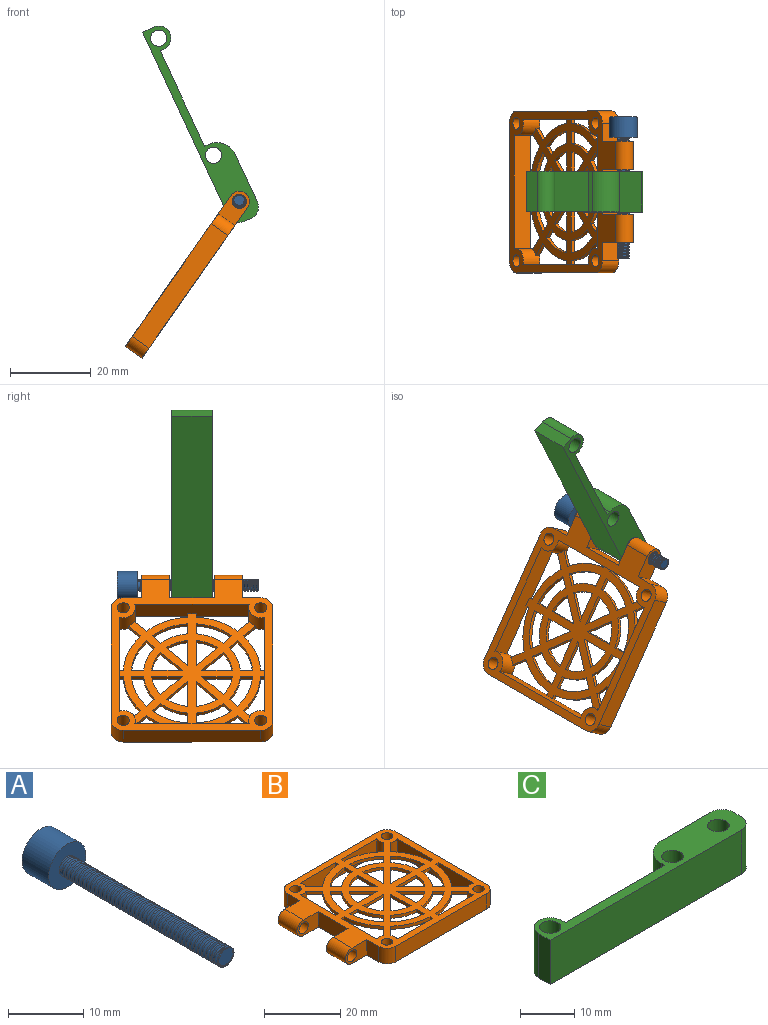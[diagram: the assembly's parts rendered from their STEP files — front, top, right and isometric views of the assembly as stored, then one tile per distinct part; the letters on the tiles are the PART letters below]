
ASSEMBLY  parts=3 mates=2
PART A: 27 faces, bbox 7x35.3x7 mm
  f0: cylinder r=1.5mm len=30mm, axis (0,1,0), area 72mm2, adj f2,f4,f24,f25,f26
  f1: plane 7x7mm, normal (0,1,0), area 16.8mm2, adj f3,f12,f13,f14,f15,f16,f17
  f2: plane 2.88x2.54mm, normal (0,-1,0), area 5.8mm2, adj f0,f24,f25
  f3: cylinder r=3.5mm len=7mm, axis (0,1,0), area 110mm2, adj f1,f4
  f4: plane 7x7mm, normal (0,-1,0), area 31.4mm2, adj f0,f3
  f5: plane 3x1.99mm, normal (-0.5,0,-0.86), area 6.9mm2, adj f6,f10,f13,f19
  f6: plane 3x2.31mm, normal (-1,0,0.01), area 6.9mm2, adj f5,f7,f12,f18
  f7: plane 3x2.01mm, normal (-0.5,0,0.87), area 6.9mm2, adj f6,f8,f14,f20
  f8: plane 3x1.99mm, normal (0.5,0,0.86), area 6.9mm2, adj f7,f9,f16,f22
  f9: plane 3x2.31mm, normal (1,0,-0.01), area 6.9mm2, adj f8,f10,f17,f23
  f10: plane 3x2.01mm, normal (0.5,0,-0.87), area 6.9mm2, adj f5,f9,f15,f21
  f11: plane 3.46x3.01mm, normal (0,1,0), area 7.8mm2, adj f18,f19,f20,f21,f22,f23
  f12: cylinder r=0.5mm len=2.89mm, axis (-0.01,0,-1), area 2mm2, adj f1,f6,f13,f14
  f13: cylinder r=0.5mm len=2.74mm, axis (0.86,0,-0.5), area 2mm2, adj f1,f5,f12,f15
  f14: cylinder r=0.5mm len=2.76mm, axis (-0.87,0,-0.5), area 2mm2, adj f1,f7,f12,f16
  f15: cylinder r=0.5mm len=2.76mm, axis (0.87,0,0.5), area 2mm2, adj f1,f10,f13,f17
  f16: cylinder r=0.5mm len=2.74mm, axis (-0.86,0,0.5), area 2mm2, adj f1,f8,f14,f17
  f17: cylinder r=0.5mm len=2.89mm, axis (0.01,0,1), area 2mm2, adj f1,f9,f15,f16
  f18: cylinder r=0.5mm len=2.31mm, axis (-0.01,0,-1), area 1.6mm2, adj f6,f11,f19,f20
  f19: cylinder r=0.5mm len=2.25mm, axis (0.86,0,-0.5), area 1.6mm2, adj f5,f11,f18,f21
  f20: cylinder r=0.5mm len=2.25mm, axis (-0.87,0,-0.5), area 1.6mm2, adj f7,f11,f18,f22
  f21: cylinder r=0.5mm len=2.25mm, axis (0.87,0,0.5), area 1.6mm2, adj f10,f11,f19,f23
  f22: cylinder r=0.5mm len=2.25mm, axis (-0.86,0,0.5), area 1.6mm2, adj f8,f11,f20,f23
  f23: cylinder r=0.5mm len=2.31mm, axis (0.01,0,1), area 1.6mm2, adj f9,f11,f21,f22
  f24: bspline ~30.18x3.46mm, area 167.6mm2, adj f0,f2,f25,f26
  f25: bspline ~30.14x3.46mm, area 176.2mm2, adj f0,f2,f24,f26
  f26: plane 0.5x0.45mm, normal (0,0,1), area 0.1mm2, adj f0,f24,f25
PART B: 113 faces, bbox 48x40x5 mm
  f0: cylinder r=3mm len=5mm, axis (0,0,-1), area 31.7mm2, adj f13,f14,f22,f23,f83,f84,f112
  f1: plane 28.34x5mm, normal (0,-1,0), area 139.7mm2, adj f2,f15,f22,f23,f74,f75,f112
  f2: cylinder r=3mm len=5mm, axis (0,0,-1), area 31.7mm2, adj f1,f3,f22,f23,f71,f72,f112
  f3: plane 28.34x5mm, normal (-1,0,0), area 139.7mm2, adj f2,f20,f22,f23,f68,f69,f112
  f4: plane 11x5mm, normal (-1,0,0), area 55mm2, adj f22,f23,f24,f26
  f5: plane 5x4.5mm, normal (-1,0,0), area 22.5mm2, adj f12,f22,f23,f25
  f6: cylinder r=3mm len=5mm, axis (0,0,-1), area 23.6mm2, adj f7,f21,f22,f23
  f7: plane 34x5mm, normal (0,-1,0), area 170mm2, adj f6,f8,f22,f23
  f8: cylinder r=3mm len=5mm, axis (0,0,-1), area 23.6mm2, adj f7,f9,f22,f23
  f9: plane 34x5mm, normal (1,0,0), area 170mm2, adj f8,f10,f22,f23
  f10: cylinder r=3mm len=5mm, axis (0,0,-1), area 23.6mm2, adj f9,f11,f22,f23
  f11: plane 34x5mm, normal (0,1,0), area 170mm2, adj f10,f12,f22,f23
  f12: cylinder r=3mm len=5mm, axis (0,0,-1), area 23.6mm2, adj f5,f11,f22,f23
  f13: plane 28.34x5mm, normal (0,1,0), area 139.7mm2, adj f0,f20,f22,f23,f86,f87,f112
  f14: plane 28.34x5mm, normal (1,0,0), area 139.7mm2, adj f0,f15,f22,f23,f80,f81,f112
  f15: cylinder r=3mm len=5mm, axis (0,0,-1), area 31.7mm2, adj f1,f14,f22,f23,f77,f78,f112
  f16: cylinder r=1.5mm len=5mm, axis (0,0,-1), area 47.1mm2, adj f22,f23
  f17: cylinder r=1.5mm len=5mm, axis (0,0,-1), area 47.1mm2, adj f22,f23
  f18: cylinder r=1.5mm len=5mm, axis (0,0,-1), area 47.1mm2, adj f22,f23
  f19: cylinder r=1.5mm len=5mm, axis (0,0,-1), area 47.1mm2, adj f22,f23
  f20: cylinder r=3mm len=5mm, axis (0,0,-1), area 31.7mm2, adj f3,f13,f22,f23,f66,f89,f112
  f21: plane 5x4.5mm, normal (-1,0,0), area 22.5mm2, adj f6,f22,f23,f27
  f22: plane 45.5x40mm, normal (0,0,1), area 969.5mm2, adj f0,f1,f2,f3,f4,f5,f6,f7
  f23: plane 45.5x40mm, normal (0,0,-1), area 400.8mm2, adj f0,f1,f2,f3,f4,f5,f6,f7
  f24: plane 8x5mm, normal (0,-1,0), area 27.7mm2, adj f4,f22,f23,f29,f31
  f25: plane 8x5mm, normal (0,1,0), area 27.7mm2, adj f5,f22,f23,f29,f31
  f26: plane 8x5mm, normal (0,1,0), area 27.7mm2, adj f4,f22,f23,f28,f30
  f27: plane 8x5mm, normal (0,-1,0), area 27.7mm2, adj f21,f22,f23,f28,f30
  f28: cylinder r=2.5mm len=7mm, axis (0,-1,0), area 55mm2, adj f22,f23,f26,f27
  f29: cylinder r=2.5mm len=7mm, axis (0,1,0), area 55mm2, adj f22,f23,f24,f25
  f30: cylinder r=1.75mm len=7mm, axis (0,1,0), area 77mm2, adj f26,f27
  f31: cylinder r=1.75mm len=7mm, axis (0,1,0), area 77mm2, adj f24,f25
  f32: cylinder r=12mm len=6.75mm, axis (0,0,1), area 7.4mm2, adj f22,f33,f111,f112
  f33: plane 2.13x2.13mm, normal (0.71,-0.71,0), area 3mm2, adj f22,f32,f34,f112
  f34: cylinder r=15mm len=8.88mm, axis (0,0,1), area 9.8mm2, adj f22,f33,f111,f112
  f35: cylinder r=12mm len=6.75mm, axis (0,0,1), area 7.4mm2, adj f22,f36,f96,f112
  f36: plane 3.01x1mm, normal (0,-1,0), area 3mm2, adj f22,f35,f37,f112
  f37: cylinder r=15mm len=8.88mm, axis (0,0,1), area 9.8mm2, adj f22,f36,f96,f112
  f38: plane 3.01x1mm, normal (1,0,0), area 3mm2, adj f22,f39,f97,f112
  f39: cylinder r=12mm len=6.75mm, axis (0,0,1), area 7.4mm2, adj f22,f38,f40,f112
  f40: plane 2.13x2.13mm, normal (-0.71,-0.71,0), area 3mm2, adj f22,f39,f97,f112
  f41: cylinder r=15mm len=8.88mm, axis (0,0,1), area 9.8mm2, adj f22,f42,f98,f112
  f42: plane 2.13x2.13mm, normal (-0.71,-0.71,0), area 3mm2, adj f22,f41,f43,f112
  f43: cylinder r=12mm len=6.75mm, axis (0,0,1), area 7.4mm2, adj f22,f42,f98,f112
  f44: cylinder r=15mm len=8.88mm, axis (0,0,1), area 9.8mm2, adj f22,f45,f99,f112
  f45: plane 3.01x1mm, normal (0,-1,0), area 3mm2, adj f22,f44,f46,f112
  f46: cylinder r=12mm len=6.75mm, axis (0,0,1), area 7.4mm2, adj f22,f45,f99,f112
  f47: cylinder r=12mm len=6.75mm, axis (0,0,1), area 7.4mm2, adj f22,f48,f100,f112
  f48: plane 3.01x1mm, normal (-1,0,0), area 3mm2, adj f22,f47,f49,f112
  f49: cylinder r=15mm len=8.88mm, axis (0,0,1), area 9.8mm2, adj f22,f48,f100,f112
  f50: plane 7.54x1mm, normal (1,0,0), area 7.5mm2, adj f22,f51,f101,f112
  f51: plane 5.33x5.33mm, normal (-0.71,-0.71,0), area 7.5mm2, adj f22,f50,f101,f112
  f52: plane 7.54x1mm, normal (0,1,0), area 7.5mm2, adj f22,f53,f102,f112
  f53: cylinder r=10mm len=5.33mm, axis (0,0,1), area 5.9mm2, adj f22,f52,f102,f112
  f54: plane 7.54x1mm, normal (-1,0,0), area 7.5mm2, adj f22,f55,f103,f112
  f55: plane 5.33x5.33mm, normal (0.71,0.71,0), area 7.5mm2, adj f22,f54,f103,f112
  f56: plane 5.33x5.33mm, normal (-0.71,0.71,0), area 7.5mm2, adj f22,f57,f104,f112
  f57: cylinder r=10mm len=5.33mm, axis (0,0,1), area 5.9mm2, adj f22,f56,f104,f112
  f58: plane 7.54x1mm, normal (-1,0,0), area 7.5mm2, adj f22,f59,f105,f112
  f59: cylinder r=10mm len=5.33mm, axis (0,0,1), area 5.9mm2, adj f22,f58,f105,f112
  f60: plane 7.54x1mm, normal (0,-1,0), area 7.5mm2, adj f22,f61,f106,f112
  f61: cylinder r=10mm len=5.33mm, axis (0,0,1), area 5.9mm2, adj f22,f60,f106,f112
  f62: plane 5.33x5.33mm, normal (0.71,-0.71,0), area 7.5mm2, adj f22,f63,f107,f112
  f63: cylinder r=10mm len=5.33mm, axis (0,0,1), area 5.9mm2, adj f22,f62,f107,f112
  f64: plane 7.54x1mm, normal (1,0,0), area 7.5mm2, adj f22,f65,f108,f112
  f65: cylinder r=10mm len=5.33mm, axis (0,0,1), area 5.9mm2, adj f22,f64,f108,f112
  f66: plane 3x3mm, normal (0.71,0.71,0), area 4.2mm2, adj f20,f22,f67,f112
  f67: cylinder r=17mm len=10.29mm, axis (0,0,1), area 11.4mm2, adj f22,f66,f68,f112
  f68: plane 1.03x1mm, normal (0,-1,0), area 1mm2, adj f3,f22,f67,f112
  f69: plane 1.03x1mm, normal (0,1,0), area 1mm2, adj f3,f22,f70,f112
  f70: cylinder r=17mm len=10.29mm, axis (0,0,1), area 11.4mm2, adj f22,f69,f71,f112
  f71: plane 3x3mm, normal (0.71,-0.71,0), area 4.2mm2, adj f2,f22,f70,f112
  f72: plane 3x3mm, normal (-0.71,0.71,0), area 4.2mm2, adj f2,f22,f73,f112
  f73: cylinder r=17mm len=10.29mm, axis (0,0,1), area 11.4mm2, adj f22,f72,f74,f112
  f74: plane 1.03x1mm, normal (1,0,0), area 1mm2, adj f1,f22,f73,f112
  f75: plane 1.03x1mm, normal (-1,0,0), area 1mm2, adj f1,f22,f76,f112
  f76: cylinder r=17mm len=10.29mm, axis (0,0,1), area 11.4mm2, adj f22,f75,f77,f112
  f77: plane 3x3mm, normal (0.71,0.71,0), area 4.2mm2, adj f15,f22,f76,f112
  f78: plane 3x3mm, normal (-0.71,-0.71,0), area 4.2mm2, adj f15,f22,f79,f112
  f79: cylinder r=17mm len=10.29mm, axis (0,0,1), area 11.4mm2, adj f22,f78,f80,f112
  f80: plane 1.03x1mm, normal (0,1,0), area 1mm2, adj f14,f22,f79,f112
  f81: plane 1.03x1mm, normal (0,-1,0), area 1mm2, adj f14,f22,f82,f112
  f82: cylinder r=17mm len=10.29mm, axis (0,0,1), area 11.4mm2, adj f22,f81,f83,f112
  f83: plane 3x3mm, normal (-0.71,0.71,0), area 4.2mm2, adj f0,f22,f82,f112
  f84: plane 3x3mm, normal (0.71,-0.71,0), area 4.2mm2, adj f0,f22,f85,f112
  f85: cylinder r=17mm len=10.29mm, axis (0,0,1), area 11.4mm2, adj f22,f84,f86,f112
  f86: plane 1.03x1mm, normal (-1,0,0), area 1mm2, adj f13,f22,f85,f112
  f87: plane 1.03x1mm, normal (1,0,0), area 1mm2, adj f13,f22,f88,f112
  f88: cylinder r=17mm len=10.29mm, axis (0,0,1), area 11.4mm2, adj f22,f87,f89,f112
  f89: plane 3x3mm, normal (-0.71,-0.71,0), area 4.2mm2, adj f20,f22,f88,f112
  f90: cylinder r=15mm len=8.88mm, axis (0,0,1), area 9.8mm2, adj f22,f91,f109,f112
  f91: plane 3.01x1mm, normal (-1,0,0), area 3mm2, adj f22,f90,f92,f112
  f92: cylinder r=12mm len=6.75mm, axis (0,0,1), area 7.4mm2, adj f22,f91,f109,f112
  f93: plane 3.01x1mm, normal (1,0,0), area 3mm2, adj f22,f94,f110,f112
  f94: cylinder r=15mm len=8.88mm, axis (0,0,1), area 9.8mm2, adj f22,f93,f95,f112
  f95: plane 2.13x2.13mm, normal (-0.71,0.71,0), area 3mm2, adj f22,f94,f110,f112
  f96: plane 2.13x2.13mm, normal (0.71,0.71,0), area 3mm2, adj f22,f35,f37,f112
  f97: cylinder r=15mm len=8.88mm, axis (0,0,1), area 9.8mm2, adj f22,f38,f40,f112
  f98: plane 3.01x1mm, normal (0,1,0), area 3mm2, adj f22,f41,f43,f112
  f99: plane 2.13x2.13mm, normal (-0.71,0.71,0), area 3mm2, adj f22,f44,f46,f112
  f100: plane 2.13x2.13mm, normal (0.71,-0.71,0), area 3mm2, adj f22,f47,f49,f112
  f101: cylinder r=10mm len=5.33mm, axis (0,0,1), area 5.9mm2, adj f22,f50,f51,f112
  f102: plane 5.33x5.33mm, normal (-0.71,-0.71,0), area 7.5mm2, adj f22,f52,f53,f112
  f103: cylinder r=10mm len=5.33mm, axis (0,0,1), area 5.9mm2, adj f22,f54,f55,f112
  f104: plane 7.54x1mm, normal (0,-1,0), area 7.5mm2, adj f22,f56,f57,f112
  f105: plane 5.33x5.33mm, normal (0.71,-0.71,0), area 7.5mm2, adj f22,f58,f59,f112
  f106: plane 5.33x5.33mm, normal (0.71,0.71,0), area 7.5mm2, adj f22,f60,f61,f112
  f107: plane 7.54x1mm, normal (0,1,0), area 7.5mm2, adj f22,f62,f63,f112
  f108: plane 5.33x5.33mm, normal (-0.71,0.71,0), area 7.5mm2, adj f22,f64,f65,f112
  f109: plane 2.13x2.13mm, normal (0.71,0.71,0), area 3mm2, adj f22,f90,f92,f112
  f110: cylinder r=12mm len=6.75mm, axis (0,0,1), area 7.4mm2, adj f22,f93,f95,f112
  f111: plane 3.01x1mm, normal (0,1,0), area 3mm2, adj f22,f32,f34,f112
  f112: plane 36x36mm, normal (0,0,-1), area 568.7mm2, adj f0,f1,f2,f3,f13,f14,f15,f20
PART C: 16 faces, bbox 53x8x10 mm
  f0: plane 10x3mm, normal (-1,0,0), area 30mm2, adj f1,f5,f8,f9
  f1: plane 50x10mm, normal (0,-1,0), area 500mm2, adj f0,f8,f9,f13
  f2: plane 10x1mm, normal (-1,0,0), area 10mm2, adj f3,f8,f9,f15
  f3: plane 26x10mm, normal (0,1,0), area 260mm2, adj f2,f4,f8,f9
  f4: plane 10x1mm, normal (1,0,0), area 10mm2, adj f3,f5,f8,f9
  f5: cylinder r=3mm len=10mm, axis (0,0,-1), area 94.2mm2, adj f0,f4,f8,f9
  f6: cylinder r=2mm len=10mm, axis (0,0,-1), area 125.7mm2, adj f8,f9
  f7: cylinder r=2mm len=10mm, axis (0,0,-1), area 125.7mm2, adj f8,f9
  f8: plane 53x8mm, normal (0,0,1), area 205.2mm2, adj f0,f1,f2,f3,f4,f5,f6,f7
  f9: plane 53x8mm, normal (0,0,-1), area 205.2mm2, adj f0,f1,f2,f3,f4,f5,f6,f7
  f10: plane 13x10mm, normal (0,1,0), area 130mm2, adj f8,f9,f12,f15
  f11: plane 10x2mm, normal (1,0,0), area 20mm2, adj f8,f9,f12,f13
  f12: cylinder r=3mm len=10mm, axis (0,0,-1), area 47.1mm2, adj f8,f9,f10,f11
  f13: cylinder r=3mm len=10mm, axis (0,0,1), area 47.1mm2, adj f1,f8,f9,f11
  f14: cylinder r=2mm len=10mm, axis (0,0,-1), area 125.7mm2, adj f8,f9
  f15: cylinder r=5mm len=10mm, axis (0,0,-1), area 78.5mm2, adj f2,f8,f9,f10
PLACE A rot(axis=(0,1,0),35deg) t=(-33.69,-74.65,45.82)mm
PLACE B rot(axis=(0,1,0),125deg) t=(-59.39,-46.23,52.27)mm
PLACE C rot(axis=(0.74,0.47,-0.47),106.8deg) t=(-14.21,-50.12,72.76)mm
MATE fastened A.f0 <-> B.f29  axis (0,-1,0) through (-51.92,-41.62,58.58)mm
MATE revolute C.f14 <-> B.f29  axis (0,-1,0) through (-51.92,-60.12,58.58)mm
